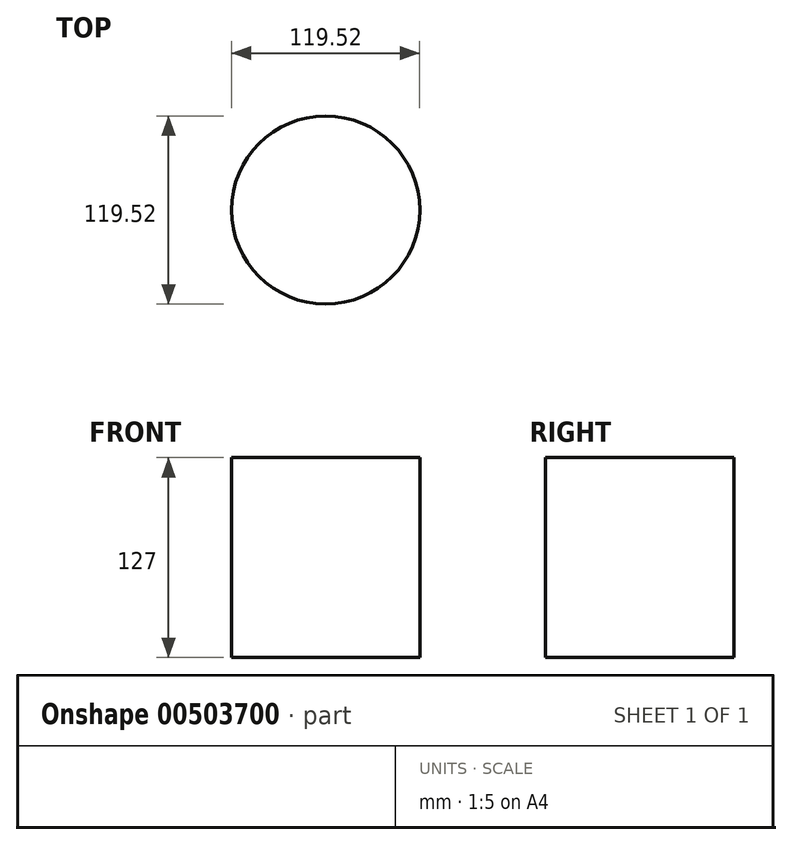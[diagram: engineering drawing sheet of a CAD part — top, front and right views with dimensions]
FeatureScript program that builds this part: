
annotation { "Feature Type Name" : "Feature", "Feature Type Description" : "" }
export const myFeature = defineFeature(function(context is Context, id is Id, definition is map)
    precondition{}
    {
        {
            var Q0;
            Q0=qCreatedBy(makeId("Top.planeOp"),FACE);
            var sketch = newSketch(context, id + "F0", { "sketchPlane" : qUnion([Q0])});
            skCircle(sketch, "E0", {"center": v(0, 0) * mm, "radius": 59.76 * mm});
            skSolve(sketch);
        }
        {
            var Q0;
            Q0=sQuery(id+"F0.wireOp",EDGE,"E0");
            extrude(context, id + "F1", {"bodyType" : ToolBodyType.SURFACE, "surfaceEntities" : qUnion([Q0]), "depth" : 127 * mm});
        }
    });
